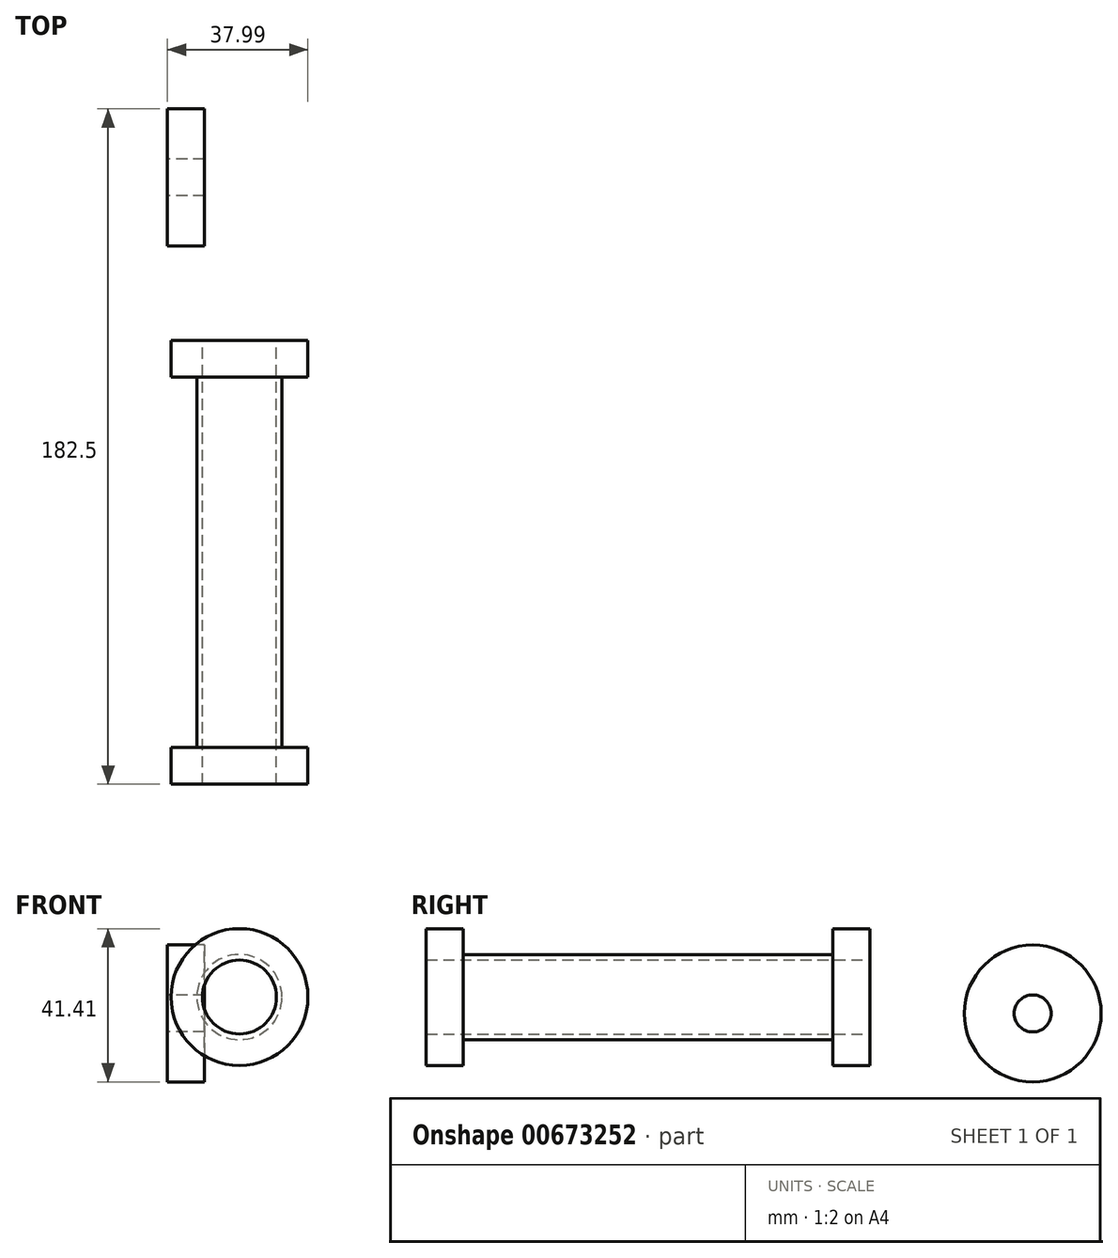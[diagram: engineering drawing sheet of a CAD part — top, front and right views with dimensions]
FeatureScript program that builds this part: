
annotation { "Feature Type Name" : "Feature", "Feature Type Description" : "" }
export const myFeature = defineFeature(function(context is Context, id is Id, definition is map)
    precondition{}
    {
        {
            var Q0;
            Q0=qCreatedBy(makeId("Front.planeOp"),FACE);
            var sketch = newSketch(context, id + "F0", { "sketchPlane" : qUnion([Q0])});
            skCircle(sketch, "E0", {"center": v(19.49, 13.62) * mm, "radius": 18.5 * mm});
            skCircle(sketch, "E1", {"center": v(19.49, 13.62) * mm, "radius": 10 * mm});
            skSolve(sketch);
        }
        {
            var Q0;
            Q0=makeQuery(id+"F0.imprint","IMPRINT",FACE,{"disambiguationData":[TD([[makeQuery(id+"F0.imprint","IMPRINT",EDGE,{"derivedFrom":sQuery(id+"F0.wireOp",EDGE,"E0")}),1.0]])]});
            var Q1;
            Q1=makeQuery(id+"F0.imprint","IMPRINT",FACE,{"disambiguationData":[TD([[makeQuery(id+"F0.imprint","IMPRINT",EDGE,{"derivedFrom":sQuery(id+"F0.wireOp",EDGE,"E1")}),1.0]])]});
            extrude(context, id + "F1", {"entities" : qUnion([Q0, Q1]), "depth" : 10 * mm, "offsetDistance" : 25 * mm});
        }
        {
            var Q0;
            Q0=makeQuery(id+"F1.opExtrude","CAP_FACE",FACE,{"disambiguationData":[OSD([sQuery(id+"F0.wireOp",EDGE,"E0")])],"isStart":false});
            var sketch = newSketch(context, id + "F2", { "sketchPlane" : qUnion([Q0])});
            skCircle(sketch, "E2", {"center": v(19.49, 13.62) * mm, "radius": 11.5 * mm});
            skSolve(sketch);
        }
        {
            var Q0;
            Q0=makeQuery(id+"F2.imprint","IMPRINT",FACE,{"disambiguationData":[TD([[makeQuery(id+"F2.imprint","IMPRINT",EDGE,{"derivedFrom":sQuery(id+"F2.wireOp",EDGE,"E2")}),1.0]])]});
            extrude(context, id + "F3", {"entities" : qUnion([Q0]), "operationType" : NewBodyOperationType.ADD, "depth" : 100 * mm, "offsetDistance" : 25 * mm});
        }
        {
            var Q0;
            Q0=makeQuery(id+"F0.imprint","IMPRINT",FACE,{"disambiguationData":[TD([[makeQuery(id+"F0.imprint","IMPRINT",EDGE,{"derivedFrom":sQuery(id+"F0.wireOp",EDGE,"E1")}),1.0]])]});
            extrude(context, id + "F4", {"entities" : qUnion([Q0]), "operationType" : NewBodyOperationType.REMOVE, "depth" : 120 * mm, "offsetDistance" : 25 * mm});
        }
        {
            var Q0;
            Q0=makeQuery(id+"F3.opExtrude","CAP_FACE",FACE,{"disambiguationData":[OSD([sQuery(id+"F2.wireOp",EDGE,"E2")])],"isStart":false});
            var sketch = newSketch(context, id + "F5", { "sketchPlane" : qUnion([Q0])});
            skCircle(sketch, "E3", {"center": v(19.49, 13.62) * mm, "radius": 18.5 * mm});
            skSolve(sketch);
        }
        {
            var Q0;
            Q0=makeQuery(id+"F5.imprint","IMPRINT",FACE,{"disambiguationData":[TD([[makeQuery(id+"F5.imprint","IMPRINT",EDGE,{"derivedFrom":sQuery(id+"F5.wireOp",EDGE,"E3")}),1.0]])]});
            var Q1;
            {var subQ0=sQuery(id+"F2.wireOp",EDGE,"E2");Q1=makeQuery(id+"F5.imprint","IMPRINT",FACE,{"disambiguationData":[TD([[makeQuery(id+"F5.imprint","IMPRINT",EDGE,{"derivedFrom":makeQuery(id+"F3.opExtrude","CAP_EDGE",EDGE,{"disambiguationData":[OSD([subQ0])],"isStart":false})}),1.0]])]});}
            extrude(context, id + "F6", {"entities" : qUnion([Q0, Q1]), "operationType" : NewBodyOperationType.ADD, "depth" : 10 * mm, "offsetDistance" : 25 * mm});
        }
        {
            var Q0;
            Q0=qCreatedBy(makeId("Right.planeOp"),FACE);
            var sketch = newSketch(context, id + "F7", { "sketchPlane" : qUnion([Q0])});
            skCircle(sketch, "E4", {"center": v(44, 9.2) * mm, "radius": 18.5 * mm});
            skCircle(sketch, "E5", {"center": v(44, 9.2) * mm, "radius": 5 * mm});
            skSolve(sketch);
        }
        {
            var Q0;
            Q0=makeQuery(id+"F7.imprint","IMPRINT",FACE,{"disambiguationData":[TD([[makeQuery(id+"F7.imprint","IMPRINT",EDGE,{"derivedFrom":sQuery(id+"F7.wireOp",EDGE,"E4")}),1.0]])]});
            extrude(context, id + "F8", {"entities" : qUnion([Q0]), "depth" : 10 * mm, "offsetDistance" : 25 * mm});
        }
    });
